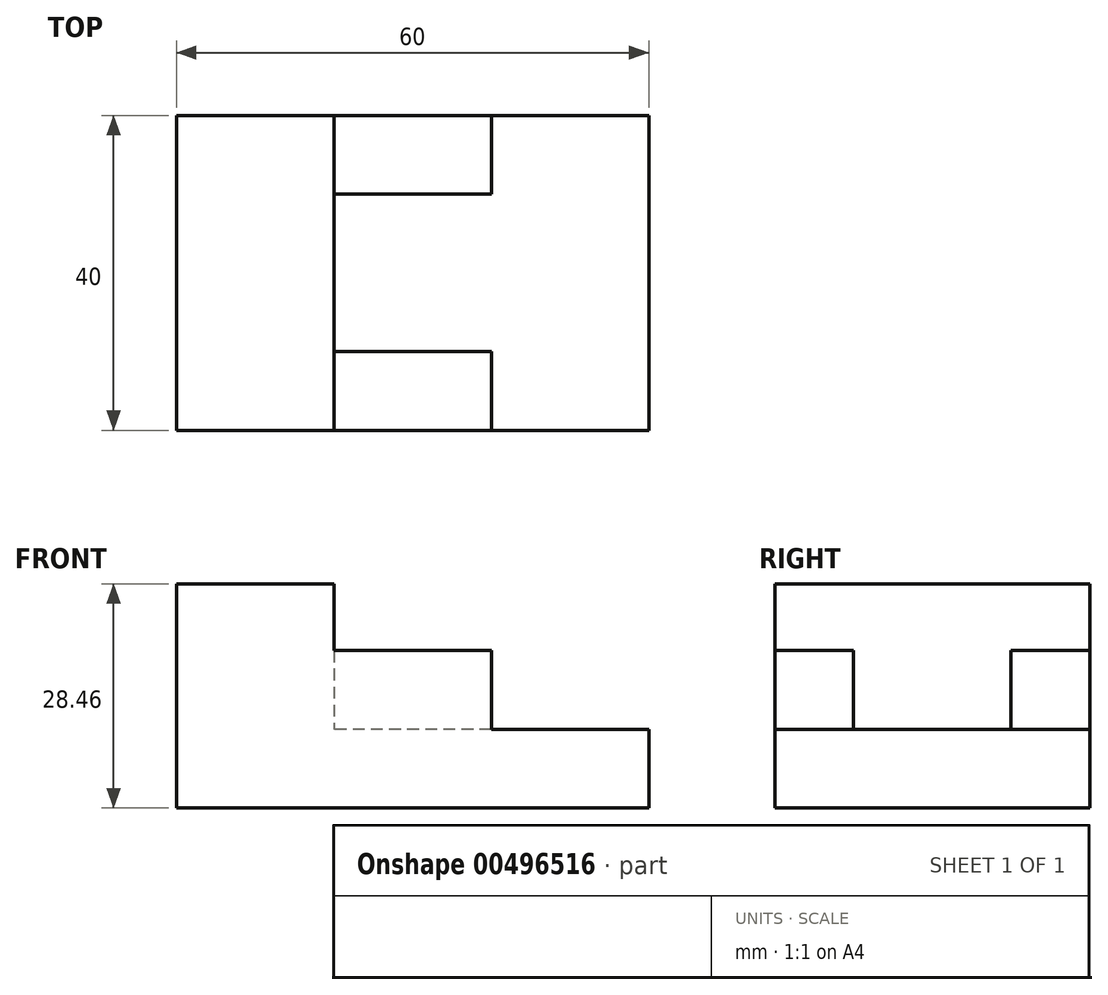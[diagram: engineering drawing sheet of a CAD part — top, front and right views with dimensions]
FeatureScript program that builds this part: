
annotation { "Feature Type Name" : "Feature", "Feature Type Description" : "" }
export const myFeature = defineFeature(function(context is Context, id is Id, definition is map)
    precondition{}
    {
        {
            var Q0;
            Q0=qCreatedBy(makeId("Front.planeOp"),FACE);
            var sketch = newSketch(context, id + "F0", { "sketchPlane" : qUnion([Q0])});
            skLineSegment(sketch, "E0", {"start": v(0, -1.54) * mm, "end": v(0, 28.46) * mm});
            skLineSegment(sketch, "E1", {"start": v(0, 0) * mm, "end": v(60, 0) * mm});
            skLineSegment(sketch, "E2", {"start": v(60, 0) * mm, "end": v(60, 10) * mm});
            skLineSegment(sketch, "E3", {"start": v(0, 28.46) * mm, "end": v(20, 28.46) * mm});
            skLineSegment(sketch, "E4", {"start": v(20, 28.46) * mm, "end": v(20, 10) * mm});
            skLineSegment(sketch, "E5", {"start": v(20, 10) * mm, "end": v(60, 10) * mm});
            skSolve(sketch);
        }
        {
            var Q0;
            Q0 = qSketchRegion(id + "F0", true);
            extrude(context, id + "F1", {"entities" : qUnion([Q0]), "depth" : 40 * mm});
        }
        {
            var Q0;
            Q0=makeQuery(id+"F1.opExtrude","SWEPT_FACE",FACE,{"disambiguationData":[OSD([sQuery(id+"F0.wireOp",EDGE,"E5")])]});
            var sketch = newSketch(context, id + "F2", { "sketchPlane" : qUnion([Q0])});
            skLineSegment(sketch, "E6", {"start": v(20, -40) * mm, "end": v(40, -40) * mm});
            skLineSegment(sketch, "E7", {"start": v(40, -40) * mm, "end": v(40, -30) * mm});
            skLineSegment(sketch, "E8", {"start": v(40, -30) * mm, "end": v(20, -30) * mm});
            skLineSegment(sketch, "E9", {"start": v(20, -30) * mm, "end": v(20, -40) * mm});
            skSolve(sketch);
        }
        {
            var Q0;
            Q0 = qSketchRegion(id + "F2", true);
            extrude(context, id + "F3", {"entities" : qUnion([Q0]), "operationType" : NewBodyOperationType.ADD, "depth" : 10 * mm});
        }
        {
            var Q0;
            Q0=makeQuery(id+"F1.opExtrude","SWEPT_FACE",FACE,{"disambiguationData":[OSD([sQuery(id+"F0.wireOp",EDGE,"E5")])]});
            var sketch = newSketch(context, id + "F4", { "sketchPlane" : qUnion([Q0])});
            skLineSegment(sketch, "E10", {"start": v(20, 0) * mm, "end": v(40, 0) * mm});
            skLineSegment(sketch, "E11", {"start": v(40, 0) * mm, "end": v(40, -10) * mm});
            skLineSegment(sketch, "E12", {"start": v(40, -10) * mm, "end": v(20, -10) * mm});
            skLineSegment(sketch, "E13", {"start": v(20, -10) * mm, "end": v(20, 0) * mm});
            skSolve(sketch);
        }
        {
            var Q0;
            Q0 = qSketchRegion(id + "F4", true);
            extrude(context, id + "F5", {"entities" : qUnion([Q0]), "operationType" : NewBodyOperationType.ADD, "depth" : 10 * mm});
        }
    });
